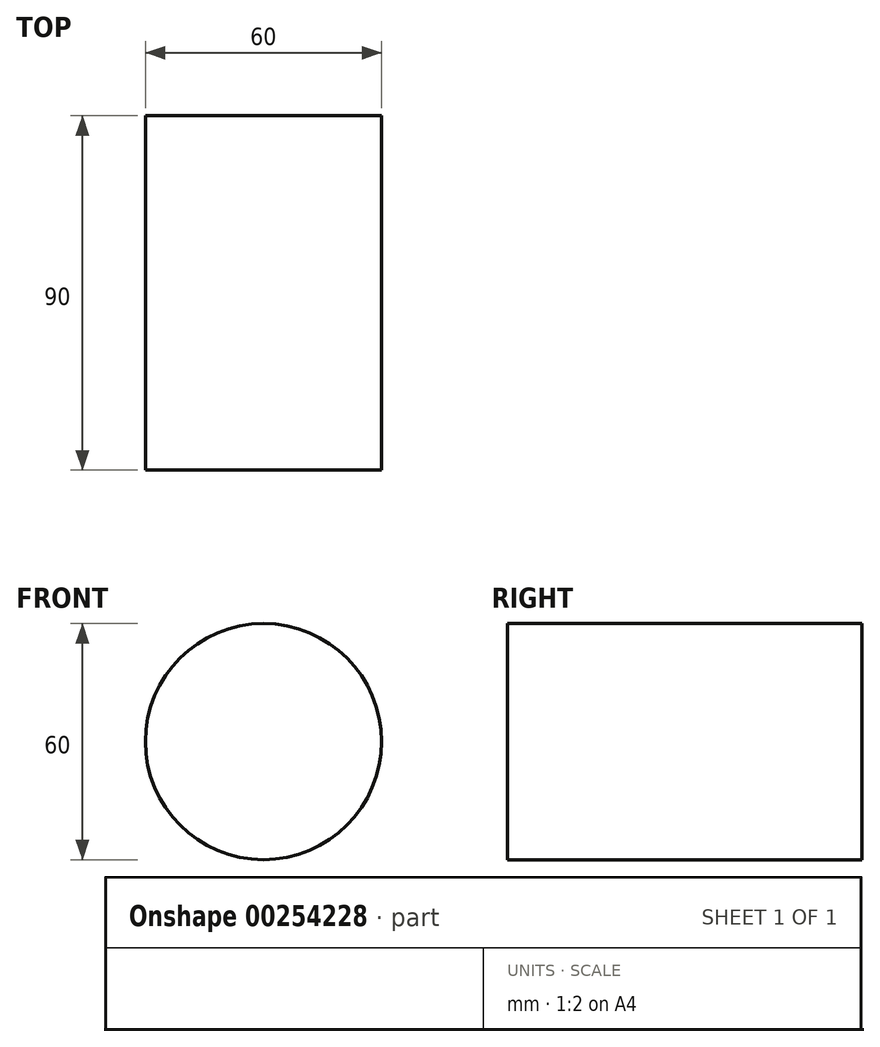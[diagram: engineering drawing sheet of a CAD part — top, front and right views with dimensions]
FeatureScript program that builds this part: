
annotation { "Feature Type Name" : "Feature", "Feature Type Description" : "" }
export const myFeature = defineFeature(function(context is Context, id is Id, definition is map)
    precondition{}
    {
        {
            var Q0;
            Q0=qCreatedBy(makeId("Front.planeOp"),FACE);
            var sketch = newSketch(context, id + "F0", { "sketchPlane" : qUnion([Q0])});
            skCircle(sketch, "E0", {"center": v(0, 0) * mm, "radius": 30 * mm});
            skSolve(sketch);
        }
        {
            var Q0;
            Q0 = qSketchRegion(id + "F0", true);
            extrude(context, id + "F1", {"entities" : qUnion([Q0]), "depth" : 90 * mm});
        }
    });
